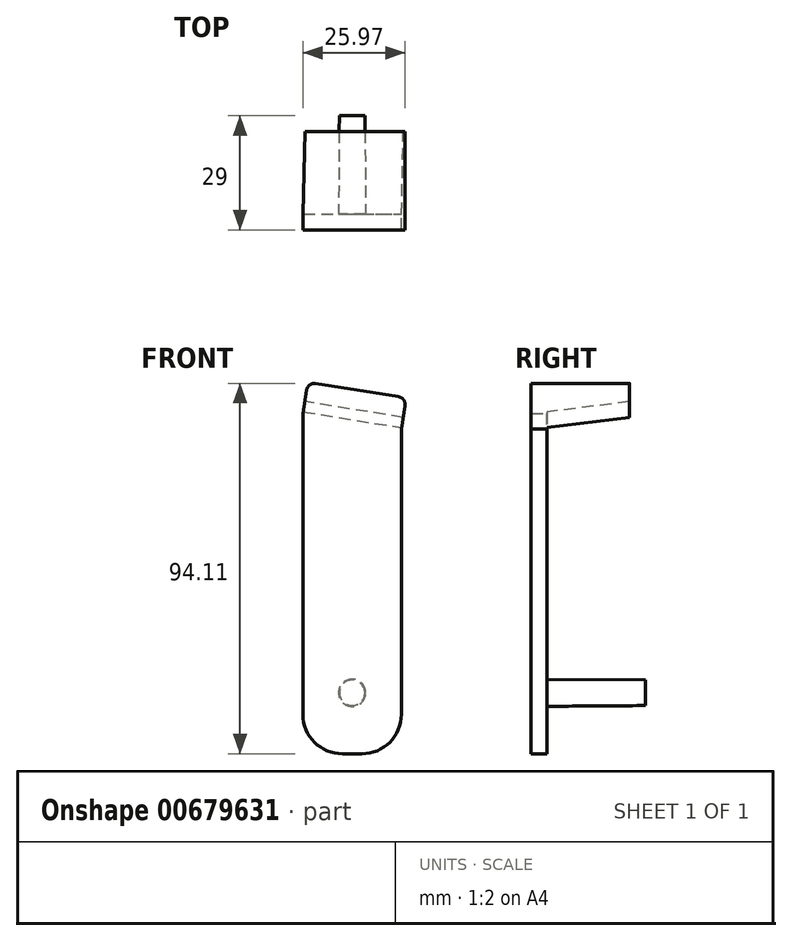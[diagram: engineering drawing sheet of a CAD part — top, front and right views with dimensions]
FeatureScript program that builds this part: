
annotation { "Feature Type Name" : "Feature", "Feature Type Description" : "" }
export const myFeature = defineFeature(function(context is Context, id is Id, definition is map)
    precondition{}
    {
        {
            var Q0;
            Q0=qCreatedBy(makeId("Front.planeOp"),FACE);
            var sketch = newSketch(context, id + "F0", { "sketchPlane" : qUnion([Q0])});
            skCircle(sketch, "E0", {"center": v(0, 0) * mm, "radius": 3.45 * mm});
            skSolve(sketch);
        }
        {
            var Q0;
            Q0 = qSketchRegion(id + "F0", true);
            extrude(context, id + "F1", {"entities" : qUnion([Q0]), "depth" : 25 * mm, "offsetDistance" : 25 * mm});
        }
        {
            var Q0;
            Q0=makeQuery(id+"F1.opExtrude","CAP_FACE",FACE,{"disambiguationData":[OSD([sQuery(id+"F0.wireOp",EDGE,"E0")])],"isStart":false});
            var sketch = newSketch(context, id + "F2", { "sketchPlane" : qUnion([Q0])});
            skLineSegment(sketch, "E1.bottom", {"start": v(-12.5, -15.5) * mm, "end": v(12.5, -15.5) * mm});
            skLineSegment(sketch, "E1.top", {"start": v(-12.5, 71) * mm, "end": v(12.5, 71) * mm});
            skLineSegment(sketch, "E1.left", {"start": v(-12.5, -15.5) * mm, "end": v(-12.5, 71) * mm});
            skLineSegment(sketch, "E1.right", {"start": v(12.5, -15.5) * mm, "end": v(12.5, 71) * mm});
            skSolve(sketch);
        }
        {
            var Q0;
            Q0 = qSketchRegion(id + "F2", true);
            extrude(context, id + "F3", {"entities" : qUnion([Q0]), "operationType" : NewBodyOperationType.ADD, "depth" : 4 * mm, "offsetDistance" : 25 * mm});
        }
        {
            var Q0;
            Q0=makeQuery(id+"F3.opExtrude","SWEPT_EDGE",EDGE,{"disambiguationData":[OSD([sQuery(id+"F2.wireOp",EDGE,"E1.top"),sQuery(id+"F2.wireOp",EDGE,"E1.right")])]});
            chamfer(context, id + "F4", {"entities" : qUnion([Q0]), "chamferType" : ChamferType.TWO_OFFSETS, "width1" : 25 * mm, "oppositeDirection" : false, "width2" : 4 * mm, "tangentPropagation" : true});
        }
        {
            var Q0;
            Q0=makeQuery(id+"F4.opChamfer","BLEND_FACE",FACE,{"disambiguationData":[OSD([sQuery(id+"F2.wireOp",EDGE,"E1.top"),sQuery(id+"F2.wireOp",EDGE,"E1.right")])]});
            var sketch = newSketch(context, id + "F5", { "sketchPlane" : qUnion([Q0])});
            skLineSegment(sketch, "E2.bottom", {"start": v(-23.56, -29) * mm, "end": v(1.76, -29) * mm});
            skLineSegment(sketch, "E2.top", {"start": v(-23.56, -4) * mm, "end": v(1.76, -4) * mm});
            skLineSegment(sketch, "E2.left", {"start": v(-23.56, -29) * mm, "end": v(-23.56, -4) * mm});
            skLineSegment(sketch, "E2.right", {"start": v(1.76, -29) * mm, "end": v(1.76, -4) * mm});
            skSolve(sketch);
        }
        {
            var Q0;
            Q0 = qSketchRegion(id + "F5", true);
            extrude(context, id + "F6", {"entities" : qUnion([Q0]), "operationType" : NewBodyOperationType.ADD, "depth" : 8 * mm, "offsetDistance" : 25 * mm});
        }
        {
            var Q0;
            Q0=makeQuery(id+"F6.opExtrude","CAP_EDGE",EDGE,{"disambiguationData":[OSD([sQuery(id+"F5.wireOp",EDGE,"E2.top")])],"isStart":true});
            chamfer(context, id + "F7", {"entities" : qUnion([Q0]), "chamferType" : ChamferType.TWO_OFFSETS, "width1" : 24 * mm, "oppositeDirection" : false, "width2" : 3 * mm, "tangentPropagation" : true});
        }
        {
            var Q0;
            Q0=makeQuery(id+"F1.opExtrude","CAP_EDGE",EDGE,{"disambiguationData":[OSD([sQuery(id+"F0.wireOp",EDGE,"E0")])],"isStart":true});
            chamfer(context, id + "F8", {"entities" : qUnion([Q0]), "chamferType" : ChamferType.TWO_OFFSETS, "width1" : 25 * mm, "oppositeDirection" : false, "width2" : .2 * mm, "tangentPropagation" : true});
        }
        {
            var Q0;
            Q0=makeQuery(id+"F3.opExtrude","SWEPT_EDGE",EDGE,{"disambiguationData":[OSD([sQuery(id+"F2.wireOp",EDGE,"E1.bottom"),sQuery(id+"F2.wireOp",EDGE,"E1.left")])]});
            var Q1;
            Q1=makeQuery(id+"F3.opExtrude","SWEPT_EDGE",EDGE,{"disambiguationData":[OSD([sQuery(id+"F2.wireOp",EDGE,"E1.bottom"),sQuery(id+"F2.wireOp",EDGE,"E1.right")])]});
            fillet(context, id + "F9", {"entities" : qUnion([Q0, Q1]), "radius" : 10 * mm, "tangentPropagation" : true, "allowEdgeOverflow" : false});
        }
        {
            var Q0;
            Q0=makeQuery(id+"F6.opExtrude","CAP_EDGE",EDGE,{"disambiguationData":[OSD([sQuery(id+"F5.wireOp",EDGE,"E2.left")])],"isStart":false});
            var Q1;
            Q1=makeQuery(id+"F6.opExtrude","CAP_EDGE",EDGE,{"disambiguationData":[OSD([sQuery(id+"F5.wireOp",EDGE,"E2.right")])],"isStart":false});
            fillet(context, id + "F10", {"entities" : qUnion([Q0, Q1]), "radius" : 2 * mm, "tangentPropagation" : true, "allowEdgeOverflow" : false});
        }
    });
